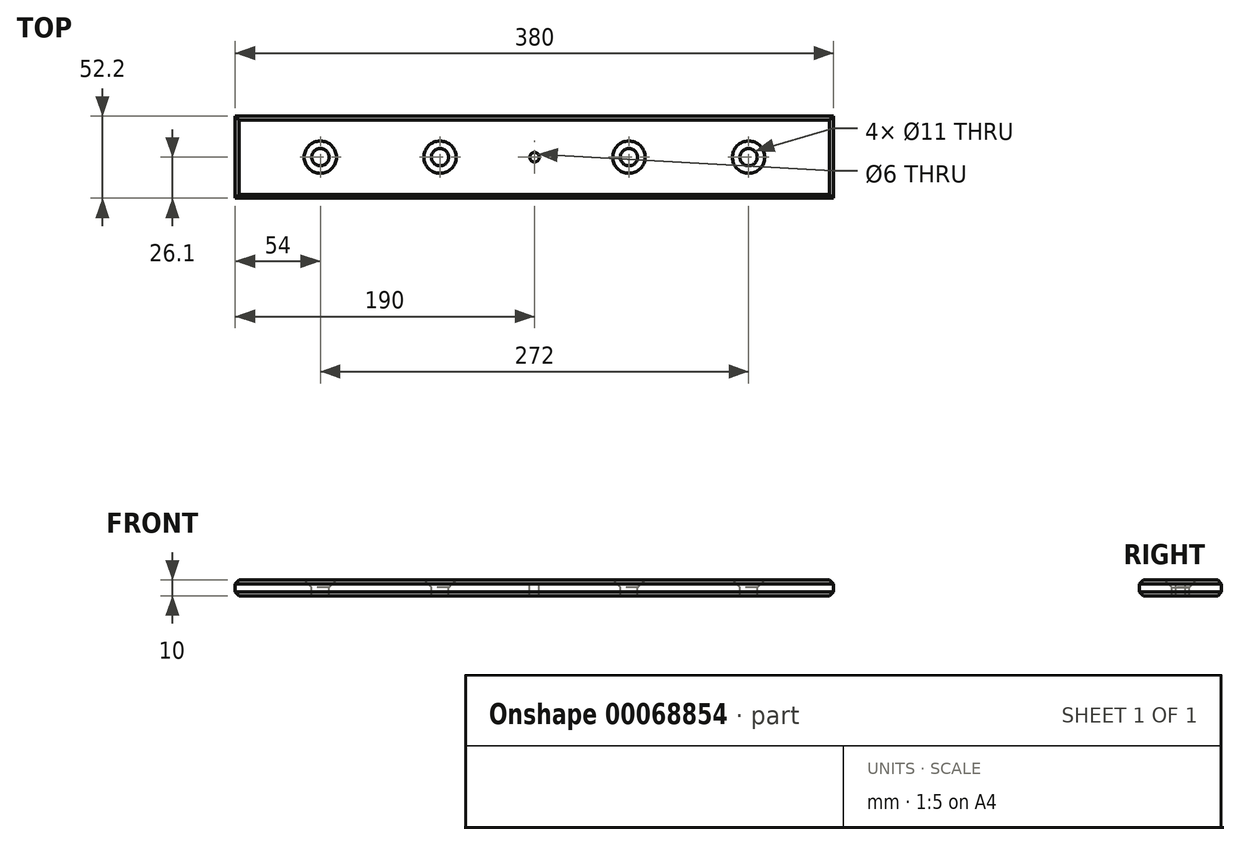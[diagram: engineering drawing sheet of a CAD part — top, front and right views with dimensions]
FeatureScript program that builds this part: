
annotation { "Feature Type Name" : "Feature", "Feature Type Description" : "" }
export const myFeature = defineFeature(function(context is Context, id is Id, definition is map)
    precondition{}
    {
        {
            var Q0;
            Q0=qCreatedBy(makeId("Top.planeOp"),FACE);
            var sketch = newSketch(context, id + "F0", { "sketchPlane" : qUnion([Q0])});
            skLineSegment(sketch, "E0.rect.bottom", {"start": v(-190, 26.1) * mm, "end": v(190, 26.1) * mm});
            skLineSegment(sketch, "E0.rect.top", {"start": v(-190, -26.1) * mm, "end": v(190, -26.1) * mm});
            skLineSegment(sketch, "E0.rect.left", {"start": v(-190, 26.1) * mm, "end": v(-190, -26.1) * mm});
            skLineSegment(sketch, "E0.rect.right", {"start": v(190, 26.1) * mm, "end": v(190, -26.1) * mm});
            skPoint(sketch, "E0.rect.middle", {"position": v(0, 0) * mm});
            skSolve(sketch);
        }
        {
            var Q0;
            Q0 = qSketchRegion(id + "F0", true);
            extrude(context, id + "F1", {"entities" : qUnion([Q0]), "endBound" : BoundingType.SYMMETRIC, "depth" : 10 * mm});
        }
        {
            var Q0;
            Q0=makeQuery(id+"F1.opExtrude","CAP_FACE",FACE,{"disambiguationData":[OSD([sQuery(id+"F0.wireOp",EDGE,"E0.rect.bottom"),sQuery(id+"F0.wireOp",EDGE,"E0.rect.top"),sQuery(id+"F0.wireOp",EDGE,"E0.rect.left"),sQuery(id+"F0.wireOp",EDGE,"E0.rect.right")])],"isStart":false});
            var Q1;
            Q1=makeQuery(id+"F1.opExtrude","CAP_FACE",FACE,{"disambiguationData":[OSD([sQuery(id+"F0.wireOp",EDGE,"E0.rect.bottom"),sQuery(id+"F0.wireOp",EDGE,"E0.rect.top"),sQuery(id+"F0.wireOp",EDGE,"E0.rect.left"),sQuery(id+"F0.wireOp",EDGE,"E0.rect.right")])],"isStart":true});
            chamfer(context, id + "F2", {"entities" : qUnion([Q0, Q1]), "width" : 2.5 * mm, "tangentPropagation" : true});
        }
        {
            var Q0;
            Q0=makeQuery(id+"F1.opExtrude","CAP_FACE",FACE,{"disambiguationData":[OSD([sQuery(id+"F0.wireOp",EDGE,"E0.rect.bottom"),sQuery(id+"F0.wireOp",EDGE,"E0.rect.top"),sQuery(id+"F0.wireOp",EDGE,"E0.rect.left"),sQuery(id+"F0.wireOp",EDGE,"E0.rect.right")])],"isStart":false});
            var sketch = newSketch(context, id + "F3", { "sketchPlane" : qUnion([Q0])});
            skLineSegment(sketch, "E1", {"start": v(-202.55, 0) * mm, "end": v(202.13, 0) * mm, "construction": true});
            skLineSegment(sketch, "E2", {"start": v(0, 85.5) * mm, "end": v(0, -82.15) * mm, "construction": true});
            skLineSegment(sketch, "E3.0", {"start": v(-60, 85.5) * mm, "end": v(-60, -82.15) * mm, "construction": true});
            skLineSegment(sketch, "E4.0", {"start": v(-136, 85.5) * mm, "end": v(-136, -82.15) * mm, "construction": true});
            skLineSegment(sketch, "E5.MirrorCS", {"start": v(60, 85.5) * mm, "end": v(60, -82.15) * mm, "construction": true});
            skLineSegment(sketch, "E6.MirrorCS", {"start": v(136, 85.5) * mm, "end": v(136, -82.15) * mm, "construction": true});
            skPoint(sketch, "E7", {"position": v(-136, 0) * mm});
            skPoint(sketch, "E8", {"position": v(-60, 0) * mm});
            skPoint(sketch, "E9", {"position": v(0, 0) * mm});
            skPoint(sketch, "E10", {"position": v(60, 0) * mm});
            skPoint(sketch, "E11", {"position": v(136, 0) * mm});
            skSolve(sketch);
        }
        {
            var Q0;
            Q0=sQuery(id+"F3.wireOp",VERTEX,"E9");
            var Q1;
            Q1=makeQuery(id+"F1.opExtrude","SWEPT_BODY",BODY,{"disambiguationData":[OSD([sQuery(id+"F0.wireOp",EDGE,"E0.rect.bottom"),sQuery(id+"F0.wireOp",EDGE,"E0.rect.top"),sQuery(id+"F0.wireOp",EDGE,"E0.rect.left"),sQuery(id+"F0.wireOp",EDGE,"E0.rect.right")])]});
            hole(context, id + "F4", {"style" : HoleStyle.SIMPLE, "holeDiameter" : 6 * mm, "endStyle" : HoleEndStyle.THROUGH, "locations" : qUnion([Q0]), "scope" : qUnion([Q1])});
        }
        {
            var Q0;
            Q0=sQuery(id+"F3.wireOp",VERTEX,"E7");
            var Q1;
            Q1=sQuery(id+"F3.wireOp",VERTEX,"E8");
            var Q2;
            Q2=sQuery(id+"F3.wireOp",VERTEX,"E10");
            var Q3;
            Q3=sQuery(id+"F3.wireOp",VERTEX,"E11");
            var Q4;
            Q4=makeQuery(id+"F1.opExtrude","SWEPT_BODY",BODY,{"disambiguationData":[OSD([sQuery(id+"F0.wireOp",EDGE,"E0.rect.bottom"),sQuery(id+"F0.wireOp",EDGE,"E0.rect.top"),sQuery(id+"F0.wireOp",EDGE,"E0.rect.left"),sQuery(id+"F0.wireOp",EDGE,"E0.rect.right")])]});
            hole(context, id + "F5", {"style" : HoleStyle.C_SINK, "holeDiameter" : 11 * mm, "cSinkDiameter" : 20.5 * mm, "endStyle" : HoleEndStyle.THROUGH, "locations" : qUnion([Q0, Q1, Q2, Q3]), "scope" : qUnion([Q4]), "cSinkAngle" : 90 * degree});
        }
    });
